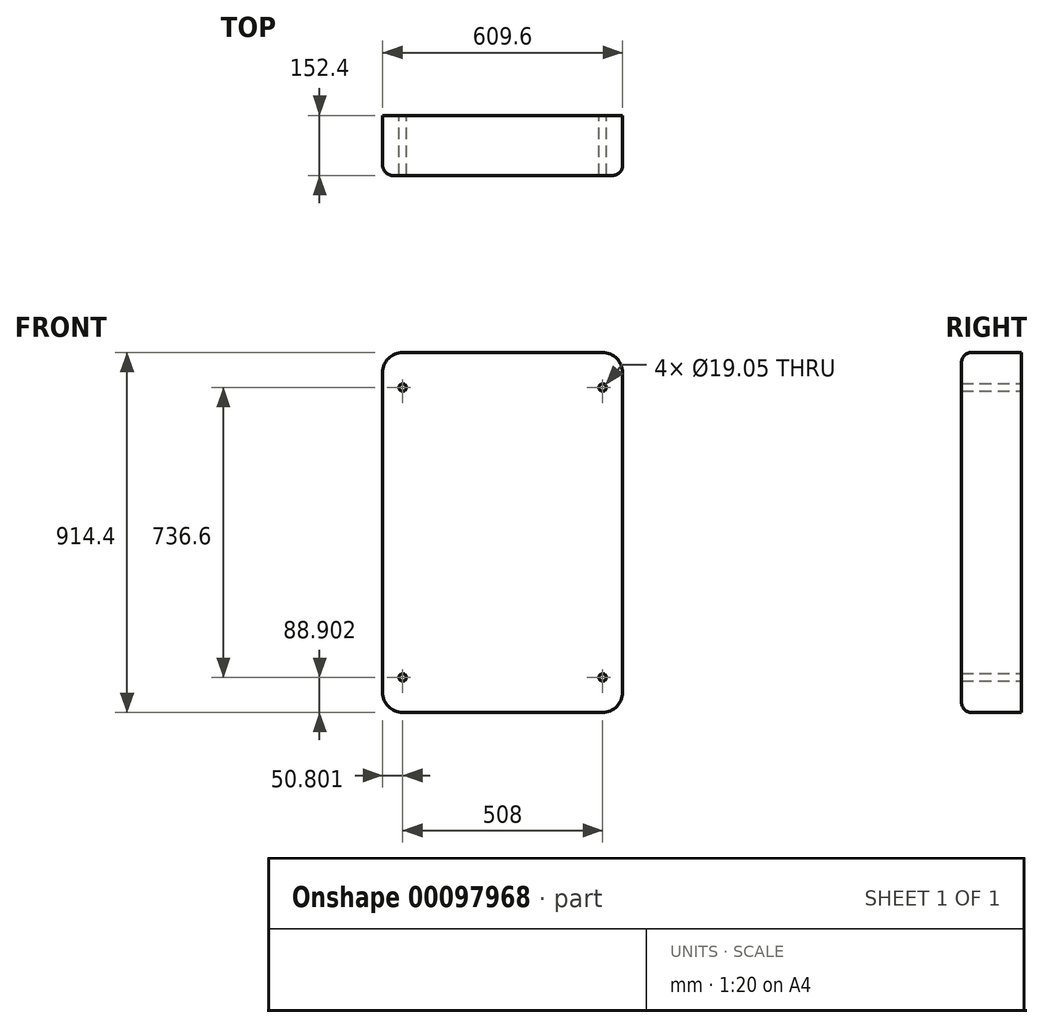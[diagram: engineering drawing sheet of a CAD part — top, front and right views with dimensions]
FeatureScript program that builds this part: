
annotation { "Feature Type Name" : "Feature", "Feature Type Description" : "" }
export const myFeature = defineFeature(function(context is Context, id is Id, definition is map)
    precondition{}
    {
        {
            var Q0;
            Q0=qCreatedBy(makeId("Front.planeOp"),FACE);
            var sketch = newSketch(context, id + "F0", { "sketchPlane" : qUnion([Q0])});
            skPoint(sketch, "E0", {"position": v(149.4, 97.32) * mm});
            skLineSegment(sketch, "E1.bottom", {"start": v(149.4, 97.32) * mm, "end": v(-358.6, 97.32) * mm, "construction": true});
            skLineSegment(sketch, "E1.top", {"start": v(149.4, -639.28) * mm, "end": v(-358.6, -639.28) * mm, "construction": true});
            skLineSegment(sketch, "E1.left", {"start": v(149.4, 97.32) * mm, "end": v(149.4, -639.28) * mm, "construction": true});
            skLineSegment(sketch, "E1.right", {"start": v(-358.6, 97.32) * mm, "end": v(-358.6, -639.28) * mm, "construction": true});
            skPoint(sketch, "E2", {"position": v(-358.6, 97.32) * mm});
            skPoint(sketch, "E3", {"position": v(-358.6, -639.28) * mm});
            skPoint(sketch, "E4", {"position": v(149.4, -639.28) * mm});
            skLineSegment(sketch, "E5.bottom", {"start": v(-409.4, 186.22) * mm, "end": v(200.2, 186.22) * mm});
            skLineSegment(sketch, "E5.top", {"start": v(-409.4, -728.18) * mm, "end": v(200.2, -728.18) * mm});
            skLineSegment(sketch, "E5.left", {"start": v(-409.4, 186.22) * mm, "end": v(-409.4, -728.18) * mm});
            skLineSegment(sketch, "E5.right", {"start": v(200.2, 186.22) * mm, "end": v(200.2, -728.18) * mm});
            skCircle(sketch, "E6", {"center": v(-358.6, 97.32) * mm, "radius": 9.53 * mm});
            skCircle(sketch, "E7", {"center": v(149.4, 97.32) * mm, "radius": 9.53 * mm});
            skCircle(sketch, "E8", {"center": v(149.4, -639.28) * mm, "radius": 9.53 * mm});
            skCircle(sketch, "E9", {"center": v(-358.6, -639.28) * mm, "radius": 9.53 * mm});
            skSolve(sketch);
        }
        {
            var Q0;
            Q0=makeQuery(id+"F0.imprint","IMPRINT",FACE,{"disambiguationData":[TD([[makeQuery(id+"F0.imprint","IMPRINT",EDGE,{"derivedFrom":sQuery(id+"F0.wireOp",EDGE,"E5.bottom")}),-1.0]])]});
            extrude(context, id + "F1", {"entities" : qUnion([Q0]), "depth" : 152.4 * mm});
        }
        {
            var Q0;
            Q0=makeQuery(id+"F1.opExtrude","SWEPT_EDGE",EDGE,{"disambiguationData":[OSD([sQuery(id+"F0.wireOp",EDGE,"E5.top"),sQuery(id+"F0.wireOp",EDGE,"E5.right")])]});
            var Q1;
            Q1=makeQuery(id+"F1.opExtrude","SWEPT_EDGE",EDGE,{"disambiguationData":[OSD([sQuery(id+"F0.wireOp",EDGE,"E5.bottom"),sQuery(id+"F0.wireOp",EDGE,"E5.right")])]});
            var Q2;
            Q2=makeQuery(id+"F1.opExtrude","SWEPT_EDGE",EDGE,{"disambiguationData":[OSD([sQuery(id+"F0.wireOp",EDGE,"E5.top"),sQuery(id+"F0.wireOp",EDGE,"E5.left")])]});
            var Q3;
            Q3=makeQuery(id+"F1.opExtrude","SWEPT_EDGE",EDGE,{"disambiguationData":[OSD([sQuery(id+"F0.wireOp",EDGE,"E5.bottom"),sQuery(id+"F0.wireOp",EDGE,"E5.left")])]});
            fillet(context, id + "F2", {"entities" : qUnion([Q0, Q1, Q2, Q3]), "radius" : 50.8 * mm, "tangentPropagation" : true, "allowEdgeOverflow" : false});
        }
        {
            var Q0;
            Q0=makeQuery(id+"F1.opExtrude","CAP_EDGE",EDGE,{"disambiguationData":[OSD([sQuery(id+"F0.wireOp",EDGE,"E5.left")])],"isStart":false});
            var Q1;
            {var subQ0=sQuery(id+"F0.wireOp",EDGE,"E5.left");var subQ1=sQuery(id+"F0.wireOp",EDGE,"E5.top");Q1=makeQuery(id+"F2.opFillet","BLEND_EDGE",EDGE,{"blendedFrom":[makeQuery(id+"F1.opExtrude","SWEPT_EDGE",EDGE,{"disambiguationData":[OSD([subQ1,subQ0])]}),makeQuery(id+"F1.opExtrude","CAP_FACE",FACE,{"disambiguationData":[OSD([sQuery(id+"F0.wireOp",EDGE,"E5.bottom"),subQ1,subQ0,sQuery(id+"F0.wireOp",EDGE,"E5.right"),sQuery(id+"F0.wireOp",EDGE,"E6"),sQuery(id+"F0.wireOp",EDGE,"E7"),sQuery(id+"F0.wireOp",EDGE,"E8"),sQuery(id+"F0.wireOp",EDGE,"E9")])],"isStart":false})],"blendedInto":[makeQuery(id+"F1.opExtrude","CAP_FACE",FACE,{"disambiguationData":[OSD([sQuery(id+"F0.wireOp",EDGE,"E5.bottom"),subQ1,subQ0,sQuery(id+"F0.wireOp",EDGE,"E5.right"),sQuery(id+"F0.wireOp",EDGE,"E6"),sQuery(id+"F0.wireOp",EDGE,"E7"),sQuery(id+"F0.wireOp",EDGE,"E8"),sQuery(id+"F0.wireOp",EDGE,"E9")])],"isStart":false})]});}
            var Q2;
            Q2=makeQuery(id+"F1.opExtrude","CAP_EDGE",EDGE,{"disambiguationData":[OSD([sQuery(id+"F0.wireOp",EDGE,"E5.top")])],"isStart":false});
            var Q3;
            {var subQ0=sQuery(id+"F0.wireOp",EDGE,"E5.right");var subQ1=sQuery(id+"F0.wireOp",EDGE,"E5.top");Q3=makeQuery(id+"F2.opFillet","BLEND_EDGE",EDGE,{"blendedFrom":[makeQuery(id+"F1.opExtrude","SWEPT_EDGE",EDGE,{"disambiguationData":[OSD([subQ1,subQ0])]}),makeQuery(id+"F1.opExtrude","CAP_FACE",FACE,{"disambiguationData":[OSD([sQuery(id+"F0.wireOp",EDGE,"E5.bottom"),subQ1,sQuery(id+"F0.wireOp",EDGE,"E5.left"),subQ0,sQuery(id+"F0.wireOp",EDGE,"E6"),sQuery(id+"F0.wireOp",EDGE,"E7"),sQuery(id+"F0.wireOp",EDGE,"E8"),sQuery(id+"F0.wireOp",EDGE,"E9")])],"isStart":false})],"blendedInto":[makeQuery(id+"F1.opExtrude","CAP_FACE",FACE,{"disambiguationData":[OSD([sQuery(id+"F0.wireOp",EDGE,"E5.bottom"),subQ1,sQuery(id+"F0.wireOp",EDGE,"E5.left"),subQ0,sQuery(id+"F0.wireOp",EDGE,"E6"),sQuery(id+"F0.wireOp",EDGE,"E7"),sQuery(id+"F0.wireOp",EDGE,"E8"),sQuery(id+"F0.wireOp",EDGE,"E9")])],"isStart":false})]});}
            var Q4;
            Q4=makeQuery(id+"F1.opExtrude","CAP_EDGE",EDGE,{"disambiguationData":[OSD([sQuery(id+"F0.wireOp",EDGE,"E5.right")])],"isStart":false});
            var Q5;
            Q5=makeQuery(id+"F1.opExtrude","CAP_EDGE",EDGE,{"disambiguationData":[OSD([sQuery(id+"F0.wireOp",EDGE,"E5.bottom")])],"isStart":false});
            var Q6;
            {var subQ0=sQuery(id+"F0.wireOp",EDGE,"E5.right");var subQ1=sQuery(id+"F0.wireOp",EDGE,"E5.bottom");Q6=makeQuery(id+"F2.opFillet","BLEND_EDGE",EDGE,{"blendedFrom":[makeQuery(id+"F1.opExtrude","SWEPT_EDGE",EDGE,{"disambiguationData":[OSD([subQ1,subQ0])]}),makeQuery(id+"F1.opExtrude","CAP_FACE",FACE,{"disambiguationData":[OSD([subQ1,sQuery(id+"F0.wireOp",EDGE,"E5.top"),sQuery(id+"F0.wireOp",EDGE,"E5.left"),subQ0,sQuery(id+"F0.wireOp",EDGE,"E6"),sQuery(id+"F0.wireOp",EDGE,"E7"),sQuery(id+"F0.wireOp",EDGE,"E8"),sQuery(id+"F0.wireOp",EDGE,"E9")])],"isStart":false})],"blendedInto":[makeQuery(id+"F1.opExtrude","CAP_FACE",FACE,{"disambiguationData":[OSD([subQ1,sQuery(id+"F0.wireOp",EDGE,"E5.top"),sQuery(id+"F0.wireOp",EDGE,"E5.left"),subQ0,sQuery(id+"F0.wireOp",EDGE,"E6"),sQuery(id+"F0.wireOp",EDGE,"E7"),sQuery(id+"F0.wireOp",EDGE,"E8"),sQuery(id+"F0.wireOp",EDGE,"E9")])],"isStart":false})]});}
            var Q7;
            {var subQ0=sQuery(id+"F0.wireOp",EDGE,"E5.left");var subQ1=sQuery(id+"F0.wireOp",EDGE,"E5.bottom");Q7=makeQuery(id+"F2.opFillet","BLEND_EDGE",EDGE,{"blendedFrom":[makeQuery(id+"F1.opExtrude","SWEPT_EDGE",EDGE,{"disambiguationData":[OSD([subQ1,subQ0])]}),makeQuery(id+"F1.opExtrude","CAP_FACE",FACE,{"disambiguationData":[OSD([subQ1,sQuery(id+"F0.wireOp",EDGE,"E5.top"),subQ0,sQuery(id+"F0.wireOp",EDGE,"E5.right"),sQuery(id+"F0.wireOp",EDGE,"E6"),sQuery(id+"F0.wireOp",EDGE,"E7"),sQuery(id+"F0.wireOp",EDGE,"E8"),sQuery(id+"F0.wireOp",EDGE,"E9")])],"isStart":false})],"blendedInto":[makeQuery(id+"F1.opExtrude","CAP_FACE",FACE,{"disambiguationData":[OSD([subQ1,sQuery(id+"F0.wireOp",EDGE,"E5.top"),subQ0,sQuery(id+"F0.wireOp",EDGE,"E5.right"),sQuery(id+"F0.wireOp",EDGE,"E6"),sQuery(id+"F0.wireOp",EDGE,"E7"),sQuery(id+"F0.wireOp",EDGE,"E8"),sQuery(id+"F0.wireOp",EDGE,"E9")])],"isStart":false})]});}
            fillet(context, id + "F3", {"entities" : qUnion([Q0, Q1, Q2, Q3, Q4, Q5, Q6, Q7]), "radius" : 25.4 * mm, "tangentPropagation" : true, "allowEdgeOverflow" : false});
        }
    });
